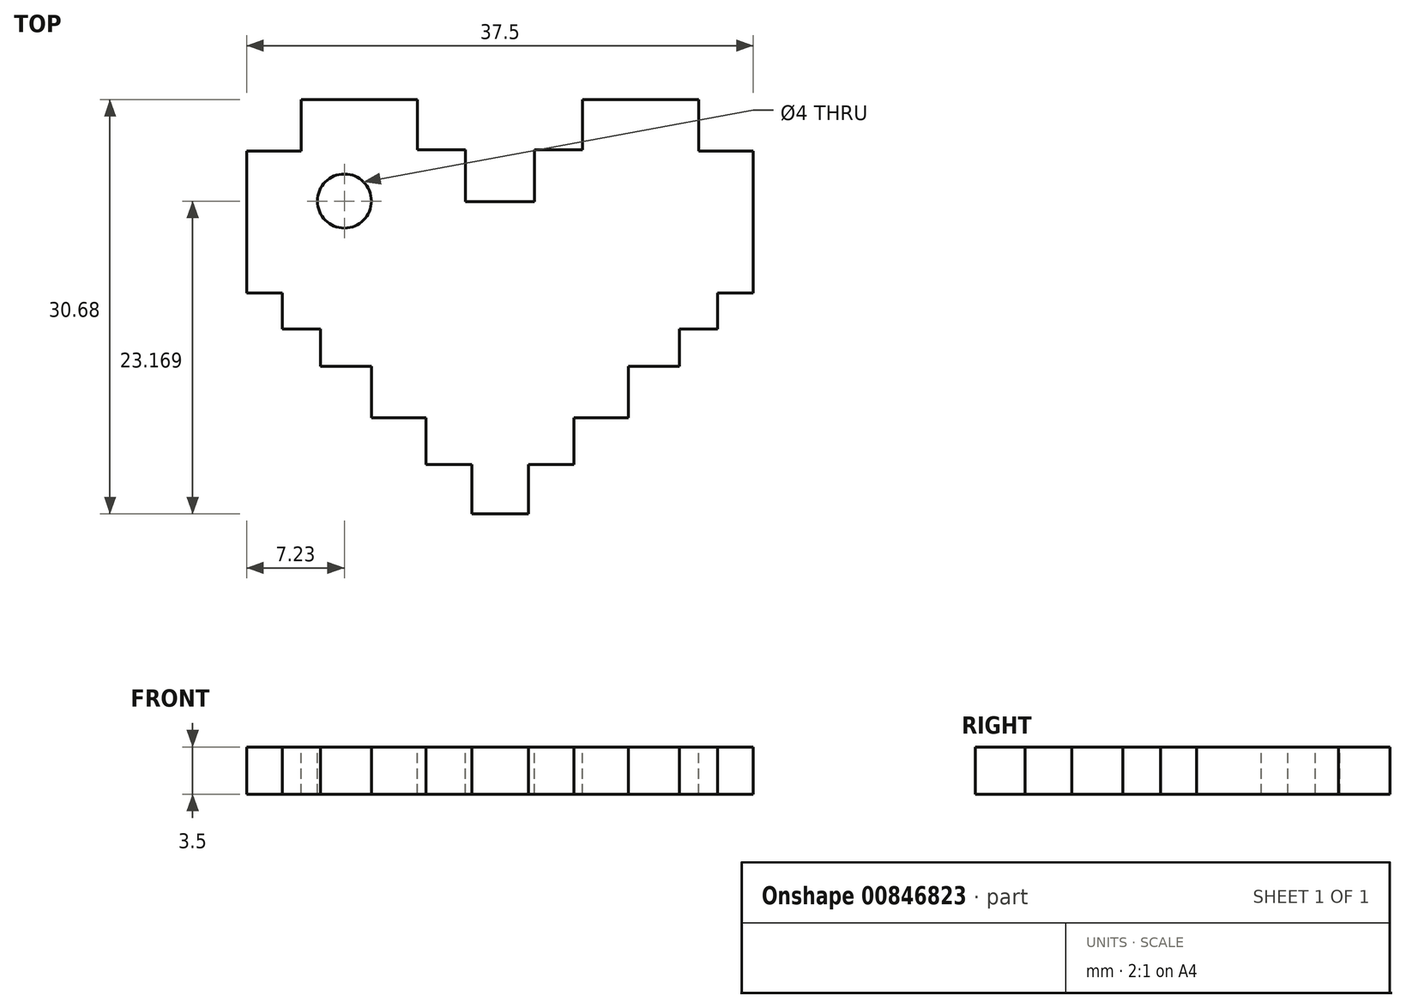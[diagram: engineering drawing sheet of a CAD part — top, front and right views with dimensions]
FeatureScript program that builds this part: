
annotation { "Feature Type Name" : "Feature", "Feature Type Description" : "" }
export const myFeature = defineFeature(function(context is Context, id is Id, definition is map)
    precondition{}
    {
        {
            var Q0;
            Q0=qCreatedBy(makeId("Top.planeOp"),FACE);
            var sketch = newSketch(context, id + "F0", { "sketchPlane" : qUnion([Q0])});
            skLineSegment(sketch, "E0", {"start": v(-18.75, 0) * mm, "end": v(18.75, 0) * mm, "construction": true});
            skLineSegment(sketch, "E1", {"start": v(0, 0) * mm, "end": v(0, 42.59) * mm, "construction": true});
            skSolve(sketch);
        }
        {
            var Q0;
            Q0=qCreatedBy(makeId("Top.planeOp"),FACE);
            var sketch = newSketch(context, id + "F1", { "sketchPlane" : qUnion([Q0])});
            skLineSegment(sketch, "E2", {"start": v(-18.75, 0) * mm, "end": v(-18.75, 5.7) * mm});
            skLineSegment(sketch, "E3", {"start": v(-18.75, 5.7) * mm, "end": v(-14.71, 5.7) * mm});
            skLineSegment(sketch, "E4", {"start": v(-14.71, 5.7) * mm, "end": v(-14.71, 9.5) * mm});
            skLineSegment(sketch, "E5", {"start": v(-14.71, 9.5) * mm, "end": v(-6.12, 9.5) * mm});
            skLineSegment(sketch, "E6", {"start": v(-6.12, 9.5) * mm, "end": v(-6.12, 5.8) * mm});
            skLineSegment(sketch, "E7", {"start": v(-6.12, 5.8) * mm, "end": v(-2.55, 5.8) * mm});
            skLineSegment(sketch, "E8", {"start": v(-2.55, 5.8) * mm, "end": v(-2.55, 1.95) * mm});
            skLineSegment(sketch, "E9", {"start": v(-2.55, 1.95) * mm, "end": v(0, 1.95) * mm});
            skLineSegment(sketch, "E10", {"start": v(-18.75, 0) * mm, "end": v(-18.75, -4.82) * mm});
            skLineSegment(sketch, "E11", {"start": v(-18.75, -4.82) * mm, "end": v(-16.1, -4.82) * mm});
            skLineSegment(sketch, "E12", {"start": v(-16.1, -4.82) * mm, "end": v(-16.1, -7.48) * mm});
            skLineSegment(sketch, "E13", {"start": v(-16.1, -7.48) * mm, "end": v(-13.28, -7.48) * mm});
            skLineSegment(sketch, "E14", {"start": v(-13.28, -7.48) * mm, "end": v(-13.28, -10.26) * mm});
            skLineSegment(sketch, "E15", {"start": v(-13.28, -10.26) * mm, "end": v(-9.5, -10.26) * mm});
            skLineSegment(sketch, "E16", {"start": v(-9.5, -10.26) * mm, "end": v(-9.5, -14.05) * mm});
            skLineSegment(sketch, "E17", {"start": v(-9.5, -14.05) * mm, "end": v(-5.48, -14.05) * mm});
            skLineSegment(sketch, "E18", {"start": v(-5.48, -14.05) * mm, "end": v(-5.48, -17.52) * mm});
            skLineSegment(sketch, "E19", {"start": v(-5.48, -17.52) * mm, "end": v(-2.1, -17.52) * mm});
            skLineSegment(sketch, "E20", {"start": v(-2.1, -17.52) * mm, "end": v(-2.1, -21.18) * mm});
            skLineSegment(sketch, "E21", {"start": v(-2.1, -21.18) * mm, "end": v(0, -21.18) * mm});
            skLineSegment(sketch, "E22.MirrorCS", {"start": v(2.1, -21.18) * mm, "end": v(0, -21.18) * mm});
            skLineSegment(sketch, "E23.MirrorCS", {"start": v(14.71, 5.7) * mm, "end": v(14.71, 9.5) * mm});
            skLineSegment(sketch, "E24.MirrorCS", {"start": v(16.1, -7.48) * mm, "end": v(13.28, -7.48) * mm});
            skLineSegment(sketch, "E25.MirrorCS", {"start": v(18.75, 0) * mm, "end": v(18.75, -4.82) * mm});
            skLineSegment(sketch, "E26.MirrorCS", {"start": v(18.75, 5.7) * mm, "end": v(14.71, 5.7) * mm});
            skLineSegment(sketch, "E27.MirrorCS", {"start": v(2.55, 1.95) * mm, "end": v(0, 1.95) * mm});
            skLineSegment(sketch, "E28.MirrorCS", {"start": v(6.12, 9.5) * mm, "end": v(6.12, 5.8) * mm});
            skLineSegment(sketch, "E29.MirrorCS", {"start": v(18.75, 0) * mm, "end": v(18.75, 5.7) * mm});
            skLineSegment(sketch, "E30.MirrorCS", {"start": v(14.71, 9.5) * mm, "end": v(6.12, 9.5) * mm});
            skLineSegment(sketch, "E31.MirrorCS", {"start": v(18.75, -4.82) * mm, "end": v(16.1, -4.82) * mm});
            skLineSegment(sketch, "E32.MirrorCS", {"start": v(16.1, -4.82) * mm, "end": v(16.1, -7.48) * mm});
            skLineSegment(sketch, "E33.MirrorCS", {"start": v(6.12, 5.8) * mm, "end": v(2.55, 5.8) * mm});
            skLineSegment(sketch, "E34.MirrorCS", {"start": v(5.48, -14.05) * mm, "end": v(5.48, -17.52) * mm});
            skLineSegment(sketch, "E35.MirrorCS", {"start": v(13.28, -7.48) * mm, "end": v(13.28, -10.26) * mm});
            skLineSegment(sketch, "E36.MirrorCS", {"start": v(2.1, -17.52) * mm, "end": v(2.1, -21.18) * mm});
            skLineSegment(sketch, "E37.MirrorCS", {"start": v(13.28, -10.26) * mm, "end": v(9.5, -10.26) * mm});
            skLineSegment(sketch, "E38.MirrorCS", {"start": v(2.55, 5.8) * mm, "end": v(2.55, 1.95) * mm});
            skLineSegment(sketch, "E39.MirrorCS", {"start": v(9.5, -10.26) * mm, "end": v(9.5, -14.05) * mm});
            skLineSegment(sketch, "E40.MirrorCS", {"start": v(5.48, -17.52) * mm, "end": v(2.1, -17.52) * mm});
            skLineSegment(sketch, "E41.MirrorCS", {"start": v(9.5, -14.05) * mm, "end": v(5.48, -14.05) * mm});
            skSolve(sketch);
        }
        {
            var Q0;
            Q0=makeQuery(id+"F1.imprint","IMPRINT",FACE,{"disambiguationData":[TD([[makeQuery(id+"F1.imprint","IMPRINT",EDGE,{"derivedFrom":sQuery(id+"F1.wireOp",EDGE,"E2")}),-1.0]])]});
            extrude(context, id + "F2", {"entities" : qUnion([Q0]), "endBound" : BoundingType.SYMMETRIC, "oppositeDirection" : true, "depth" : 3.5 * mm, "offsetDistance" : 25 * mm});
        }
        {
            var Q0;
            Q0=makeQuery(id+"F2.opExtrude","CAP_FACE",FACE,{"disambiguationData":[OSD([sQuery(id+"F1.wireOp",EDGE,"E2"),sQuery(id+"F1.wireOp",EDGE,"E3"),sQuery(id+"F1.wireOp",EDGE,"E4"),sQuery(id+"F1.wireOp",EDGE,"E5"),sQuery(id+"F1.wireOp",EDGE,"E6"),sQuery(id+"F1.wireOp",EDGE,"E7"),sQuery(id+"F1.wireOp",EDGE,"E8"),sQuery(id+"F1.wireOp",EDGE,"E9"),sQuery(id+"F1.wireOp",EDGE,"E10"),sQuery(id+"F1.wireOp",EDGE,"E11"),sQuery(id+"F1.wireOp",EDGE,"E12"),sQuery(id+"F1.wireOp",EDGE,"E13"),sQuery(id+"F1.wireOp",EDGE,"E14"),sQuery(id+"F1.wireOp",EDGE,"E15"),sQuery(id+"F1.wireOp",EDGE,"E16"),sQuery(id+"F1.wireOp",EDGE,"E17"),sQuery(id+"F1.wireOp",EDGE,"E18"),sQuery(id+"F1.wireOp",EDGE,"E19"),sQuery(id+"F1.wireOp",EDGE,"E20"),sQuery(id+"F1.wireOp",EDGE,"E21"),sQuery(id+"F1.wireOp",EDGE,"E22.MirrorCS"),sQuery(id+"F1.wireOp",EDGE,"E23.MirrorCS"),sQuery(id+"F1.wireOp",EDGE,"E24.MirrorCS"),sQuery(id+"F1.wireOp",EDGE,"E25.MirrorCS"),sQuery(id+"F1.wireOp",EDGE,"E26.MirrorCS"),sQuery(id+"F1.wireOp",EDGE,"E27.MirrorCS"),sQuery(id+"F1.wireOp",EDGE,"E28.MirrorCS"),sQuery(id+"F1.wireOp",EDGE,"E29.MirrorCS"),sQuery(id+"F1.wireOp",EDGE,"E30.MirrorCS"),sQuery(id+"F1.wireOp",EDGE,"E31.MirrorCS"),sQuery(id+"F1.wireOp",EDGE,"E32.MirrorCS"),sQuery(id+"F1.wireOp",EDGE,"E33.MirrorCS"),sQuery(id+"F1.wireOp",EDGE,"E34.MirrorCS"),sQuery(id+"F1.wireOp",EDGE,"E35.MirrorCS"),sQuery(id+"F1.wireOp",EDGE,"E36.MirrorCS"),sQuery(id+"F1.wireOp",EDGE,"E37.MirrorCS"),sQuery(id+"F1.wireOp",EDGE,"E38.MirrorCS"),sQuery(id+"F1.wireOp",EDGE,"E39.MirrorCS"),sQuery(id+"F1.wireOp",EDGE,"E40.MirrorCS"),sQuery(id+"F1.wireOp",EDGE,"E41.MirrorCS")])],"isStart":true});
            var sketch = newSketch(context, id + "F3", { "sketchPlane" : qUnion([Q0])});
            skCircle(sketch, "E42", {"center": v(-11.52, 1.99) * mm, "radius": 2 * mm});
            skSolve(sketch);
        }
        {
            var Q0;
            Q0=makeQuery(id+"F3.imprint","IMPRINT",FACE,{"disambiguationData":[TD([[makeQuery(id+"F3.imprint","IMPRINT",EDGE,{"derivedFrom":sQuery(id+"F3.wireOp",EDGE,"E42")}),1.0]])]});
            extrude(context, id + "F4", {"entities" : qUnion([Q0]), "operationType" : NewBodyOperationType.REMOVE, "endBound" : BoundingType.THROUGH_ALL, "oppositeDirection" : true, "depth" : 25 * mm, "offsetDistance" : 25 * mm});
        }
    });
